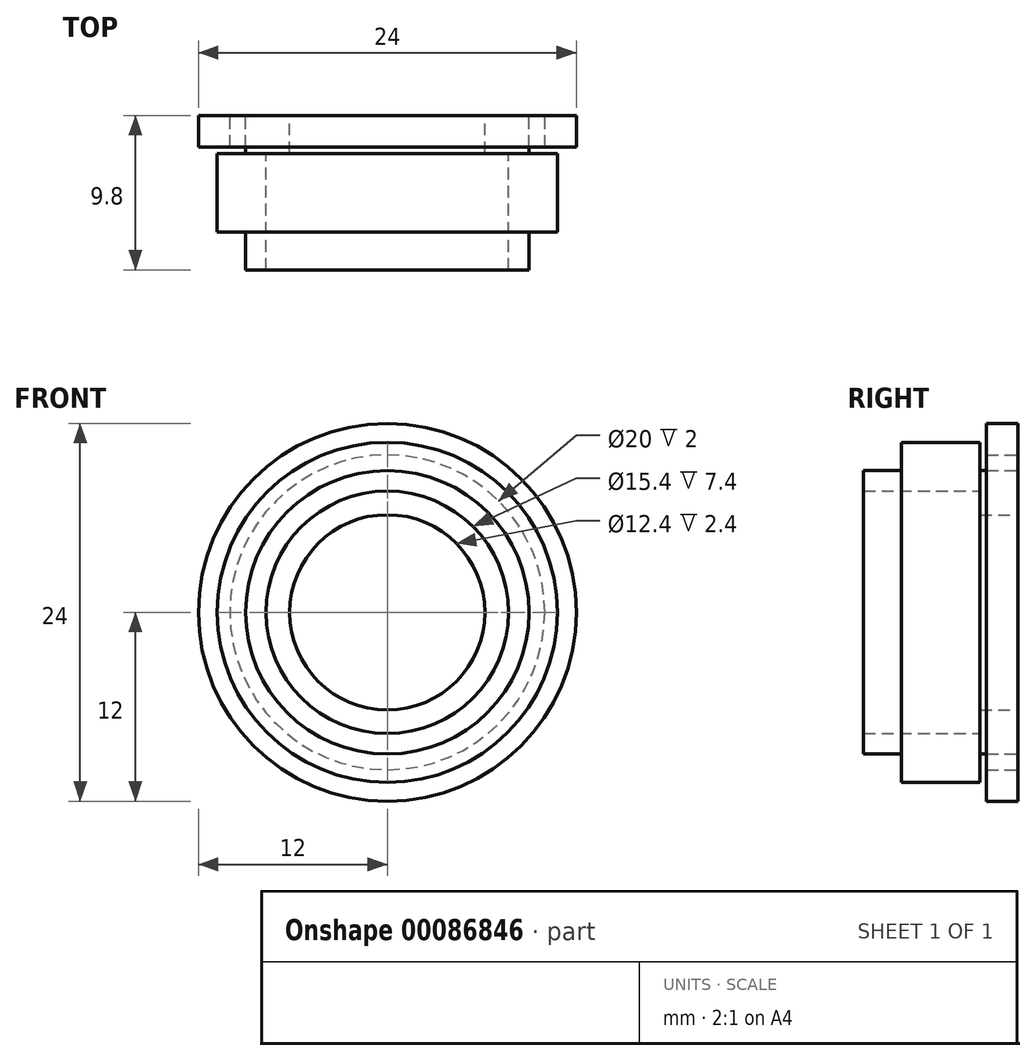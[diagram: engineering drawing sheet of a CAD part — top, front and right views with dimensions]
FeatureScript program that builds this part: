
annotation { "Feature Type Name" : "Feature", "Feature Type Description" : "" }
export const myFeature = defineFeature(function(context is Context, id is Id, definition is map)
    precondition{}
    {
        {
            var Q0;
            Q0=qCreatedBy(makeId("Front.planeOp"),FACE);
            var sketch = newSketch(context, id + "F0", { "sketchPlane" : qUnion([Q0])});
            skCircle(sketch, "E0", {"center": v(0, 0) * mm, "radius": 9 * mm});
            skCircle(sketch, "E1", {"center": v(0, 0) * mm, "radius": 10.8 * mm});
            skCircle(sketch, "E2", {"center": v(0, 0) * mm, "radius": 7.7 * mm});
            skSolve(sketch);
        }
        {
            var Q0;
            Q0=makeQuery(id+"F0.imprint","IMPRINT",FACE,{"disambiguationData":[TD([[makeQuery(id+"F0.imprint","IMPRINT",EDGE,{"derivedFrom":sQuery(id+"F0.wireOp",EDGE,"E0")}),-1.0]])]});
            extrude(context, id + "F1", {"entities" : qUnion([Q0]), "depth" : 5 * mm, "symmetric" : true});
        }
        {
            var Q0;
            Q0=makeQuery(id+"F0.imprint","IMPRINT",FACE,{"disambiguationData":[TD([[makeQuery(id+"F0.imprint","IMPRINT",EDGE,{"derivedFrom":sQuery(id+"F0.wireOp",EDGE,"E0")}),1.0]])]});
            extrude(context, id + "F2", {"entities" : qUnion([Q0]), "operationType" : NewBodyOperationType.ADD, "depth" : 9.8 * mm, "symmetric" : true});
        }
        {
            var Q0;
            Q0=makeQuery(id+"F2.opExtrude","CAP_FACE",FACE,{"disambiguationData":[OSD([sQuery(id+"F0.wireOp",EDGE,"E0"),sQuery(id+"F0.wireOp",EDGE,"E2")])],"isStart":true});
            var sketch = newSketch(context, id + "F3", { "sketchPlane" : qUnion([Q0])});
            skCircle(sketch, "E3", {"center": v(0, 0) * mm, "radius": 6.2 * mm});
            skSolve(sketch);
        }
        {
            var Q0;
            Q0=makeQuery(id+"F3.imprint","IMPRINT",FACE,{"disambiguationData":[TD([[makeQuery(id+"F3.imprint","IMPRINT",EDGE,{"derivedFrom":sQuery(id+"F3.wireOp",EDGE,"E3")}),-1.0]])]});
            extrude(context, id + "F4", {"entities" : qUnion([Q0]), "operationType" : NewBodyOperationType.ADD, "oppositeDirection" : true, "depth" : 2.4 * mm});
        }
        {
            var Q0;
            {var subQ0=sQuery(id+"F0.wireOp",EDGE,"E2");Q0=makeQuery(id+"F4.boolean.opBoolean","MERGE",FACE,{"derivedFrom":[makeQuery(id+"F2.opExtrude","CAP_FACE",FACE,{"disambiguationData":[OSD([sQuery(id+"F0.wireOp",EDGE,"E0"),subQ0])],"isStart":true}),makeQuery(id+"F4.opExtrude","CAP_FACE",FACE,{"disambiguationData":[OSD([subQ0,sQuery(id+"F3.wireOp",EDGE,"E3")])],"isStart":true})]});}
            var sketch = newSketch(context, id + "F5", { "sketchPlane" : qUnion([Q0])});
            skCircle(sketch, "E4", {"center": v(0, 0) * mm, "radius": 10 * mm});
            skCircle(sketch, "E5", {"center": v(0, 0) * mm, "radius": 12 * mm});
            skSolve(sketch);
        }
        {
            var Q0;
            Q0=makeQuery(id+"F5.imprint","IMPRINT",FACE,{"disambiguationData":[TD([[makeQuery(id+"F5.imprint","IMPRINT",EDGE,{"derivedFrom":sQuery(id+"F5.wireOp",EDGE,"E4")}),-1.0]])]});
            extrude(context, id + "F6", {"entities" : qUnion([Q0]), "oppositeDirection" : true, "depth" : 2 * mm});
        }
    });
